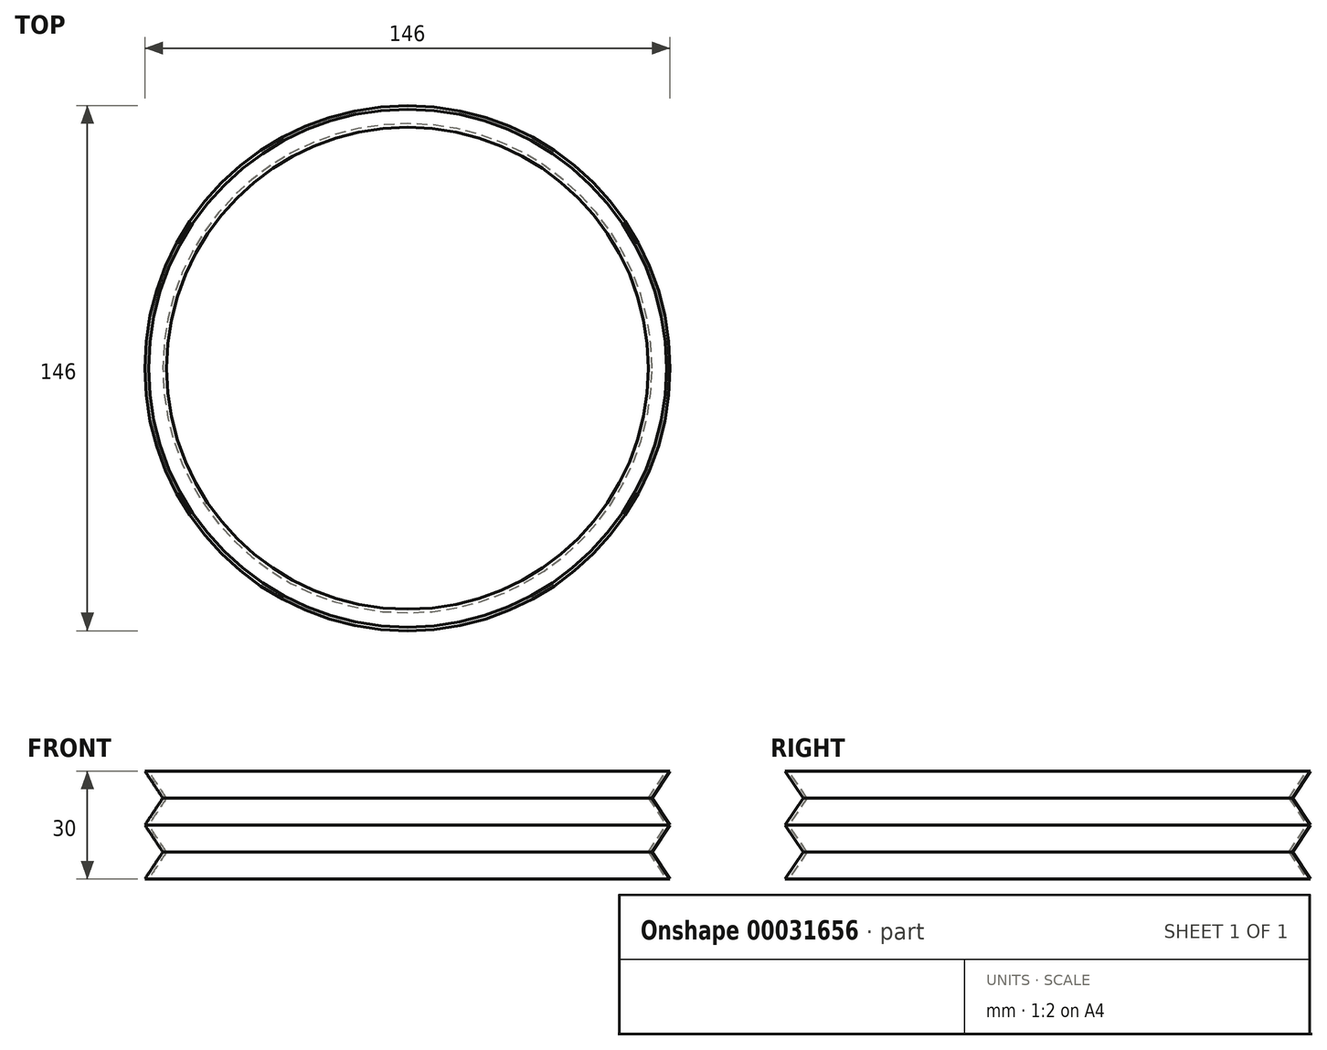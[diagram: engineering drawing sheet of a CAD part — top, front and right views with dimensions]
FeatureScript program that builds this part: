
annotation { "Feature Type Name" : "Feature", "Feature Type Description" : "" }
export const myFeature = defineFeature(function(context is Context, id is Id, definition is map)
    precondition{}
    {
        {
            var Q0;
            Q0=qCreatedBy(makeId("Front.planeOp"),FACE);
            var sketch = newSketch(context, id + "F0", { "sketchPlane" : qUnion([Q0])});
            skLineSegment(sketch, "E0", {"start": v(-73, 0) * mm, "end": v(-68, 7.5) * mm});
            skLineSegment(sketch, "E1", {"start": v(-68, 7.5) * mm, "end": v(-73, 15) * mm});
            skLineSegment(sketch, "E2", {"start": v(-73, 15) * mm, "end": v(-68, 22.5) * mm});
            skLineSegment(sketch, "E3", {"start": v(-68, 22.5) * mm, "end": v(-73, 30) * mm});
            skLineSegment(sketch, "E4.0", {"start": v(-67, 22.5) * mm, "end": v(-72, 30) * mm});
            skLineSegment(sketch, "E4.1", {"start": v(-72, 15) * mm, "end": v(-67, 22.5) * mm});
            skLineSegment(sketch, "E4.2", {"start": v(-67, 7.5) * mm, "end": v(-72, 15) * mm});
            skLineSegment(sketch, "E4.3", {"start": v(-72, 0) * mm, "end": v(-67, 7.5) * mm});
            skLineSegment(sketch, "E5", {"start": v(-73, 0) * mm, "end": v(-72, 0) * mm});
            skLineSegment(sketch, "E6", {"start": v(-73, 30) * mm, "end": v(-72, 30) * mm});
            skLineSegment(sketch, "E7", {"start": v(0, 0) * mm, "end": v(0, 31.84) * mm, "construction": true});
            skSolve(sketch);
        }
        {
            var Q0;
            Q0=makeQuery(id+"F0.imprint","IMPRINT",FACE,{"disambiguationData":[TD([[makeQuery(id+"F0.imprint","IMPRINT",EDGE,{"derivedFrom":sQuery(id+"F0.wireOp",EDGE,"E0")}),-1.0]])]});
            var Q1;
            Q1=sQuery(id+"F0.wireOp",EDGE,"E4.2");
            var Q2;
            Q2=sQuery(id+"F0.wireOp",EDGE,"E3");
            var Q3;
            Q3=sQuery(id+"F0.wireOp",EDGE,"E4.0");
            var Q4;
            Q4=sQuery(id+"F0.wireOp",EDGE,"E4.1");
            var Q5;
            Q5=sQuery(id+"F0.wireOp",EDGE,"E4.3");
            var Q6;
            Q6=sQuery(id+"F0.wireOp",EDGE,"E2");
            var Q7;
            Q7=sQuery(id+"F0.wireOp",EDGE,"E1");
            var Q8;
            Q8=sQuery(id+"F0.wireOp",EDGE,"E0");
            var Q9;
            Q9=sQuery(id+"F0.wireOp",EDGE,"E5");
            var Q10;
            Q10=sQuery(id+"F0.wireOp",EDGE,"E6");
            var Q11;
            Q11=sQuery(id+"F0.wireOp",EDGE,"E7");
            revolve(context, id + "F1", {"entities" : qUnion([Q0]), "surfaceEntities" : qUnion([Q1, Q2, Q3, Q4, Q5, Q6, Q7, Q8, Q9, Q10]), "axis" : qUnion([Q11]), "revolveType" : RevolveType.FULL});
        }
    });
